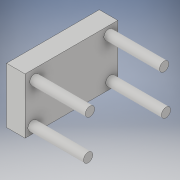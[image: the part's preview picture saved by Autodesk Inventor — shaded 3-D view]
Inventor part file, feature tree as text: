
AUTODESK INVENTOR PART (.ipt)
format: ipt  version: 2019 (Build 230136000, 136)  size: 123,392 bytes
history: native  units: in
note: dims shown in document units (in); Inventor stores cm internally (conversion verified against a paired STEP export)
features: extrude x2, sketch x2, other x1, plane x1, projected_geometry x1
ambient origin geometry x8: Origin, YZ Plane, XZ Plane, XY Plane, X Axis, Y Axis, Z Axis, Center Point
bodies: Solid1 (feature_tree)
feature tree (7):
  other  "Table"
  plane  "Work Plane1"
  extrude  "Extrusion1"  Depth=5.0in
  extrude  "Extrusion2"  Depth=1.0in TaperAngle=0.0deg
  sketch  "Sketch1"  dims[d0=0.125in d1=5.0in]
  sketch  "Sketch2"  dims[d2=3.0in d3=1.0in d4=0.0in d5=0.5in d6=0.4in d7=0.4in d8=0.4in d9=0.5in d10=0.5in d11=0.5in d12=0.5in d13=0.5in d14=0.5in d15=0.4in d16=0.4in d17=3.0in d18=0.0in]
  projected_geometry  "Projected Loop1"
